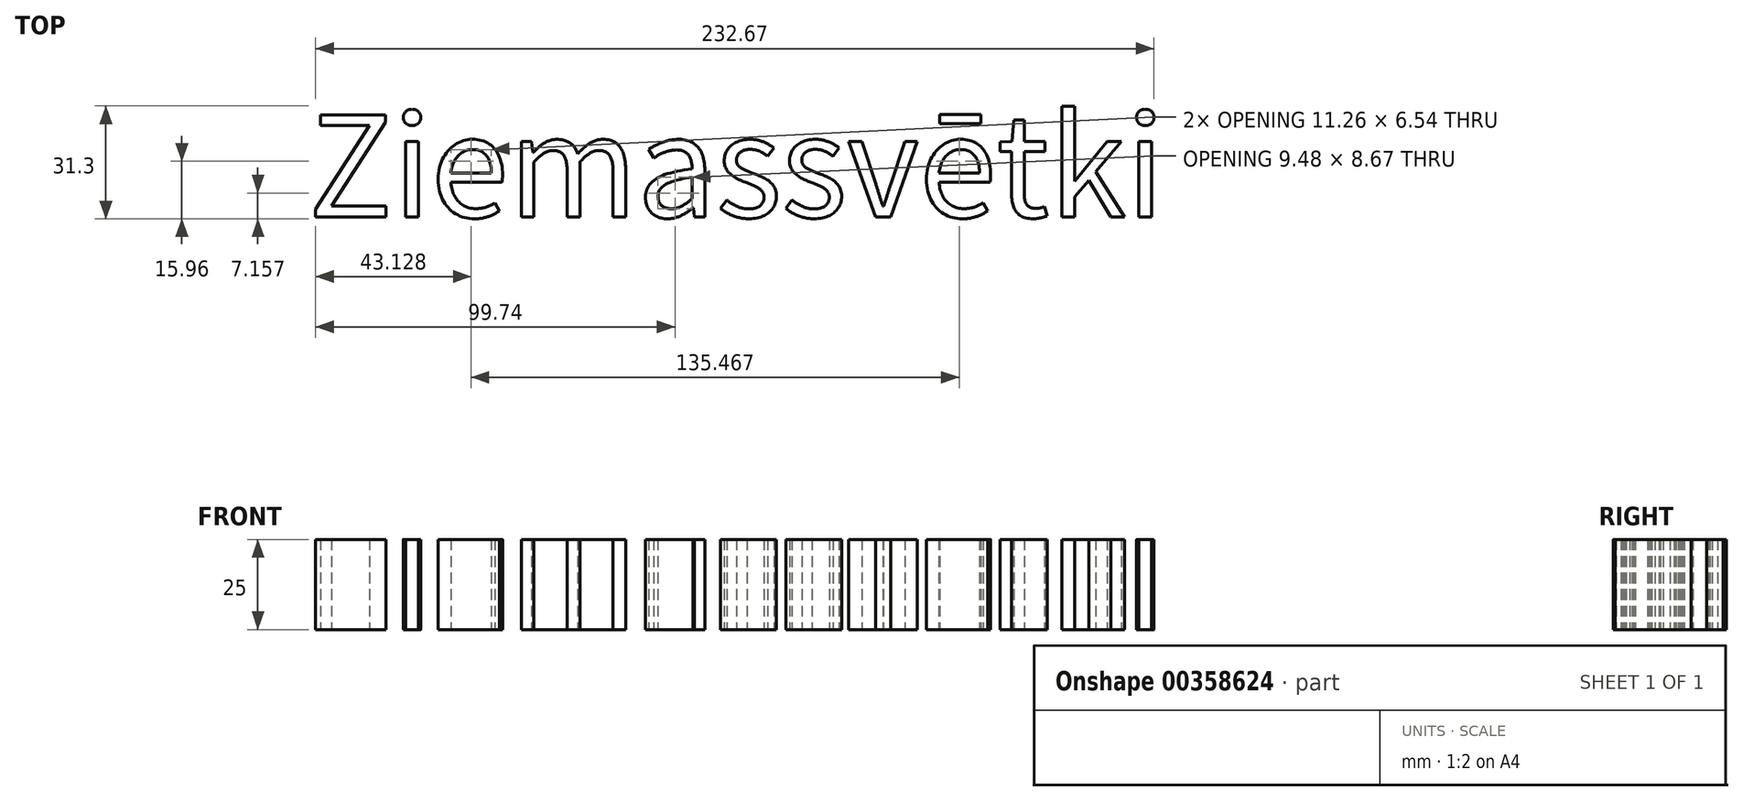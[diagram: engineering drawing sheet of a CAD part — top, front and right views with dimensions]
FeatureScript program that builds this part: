
annotation { "Feature Type Name" : "Feature", "Feature Type Description" : "" }
export const myFeature = defineFeature(function(context is Context, id is Id, definition is map)
    precondition{}
    {
        {
            var Q0;
            Q0=qCreatedBy(makeId("Top.planeOp"),FACE);
            var sketch = newSketch(context, id + "F0", { "sketchPlane" : qUnion([Q0])});
            skText(sketch, "E0", { "text": "Ziemassvētki", "fontName": "NotoSansCJKjp-Regular.otf"});
            const initialGuessF0  = {"E0": [-0.12496, -0.01575, 1, 0, 0.02786]};
            skSetInitialGuess(sketch, initialGuessF0);
            skSolve(sketch);
        }
        {
            var Q0;
            Q0 = qSketchRegion(id + "F0", true);
            extrude(context, id + "F1", {"entities" : qUnion([Q0]), "depth" : 25 * mm});
        }
    });
